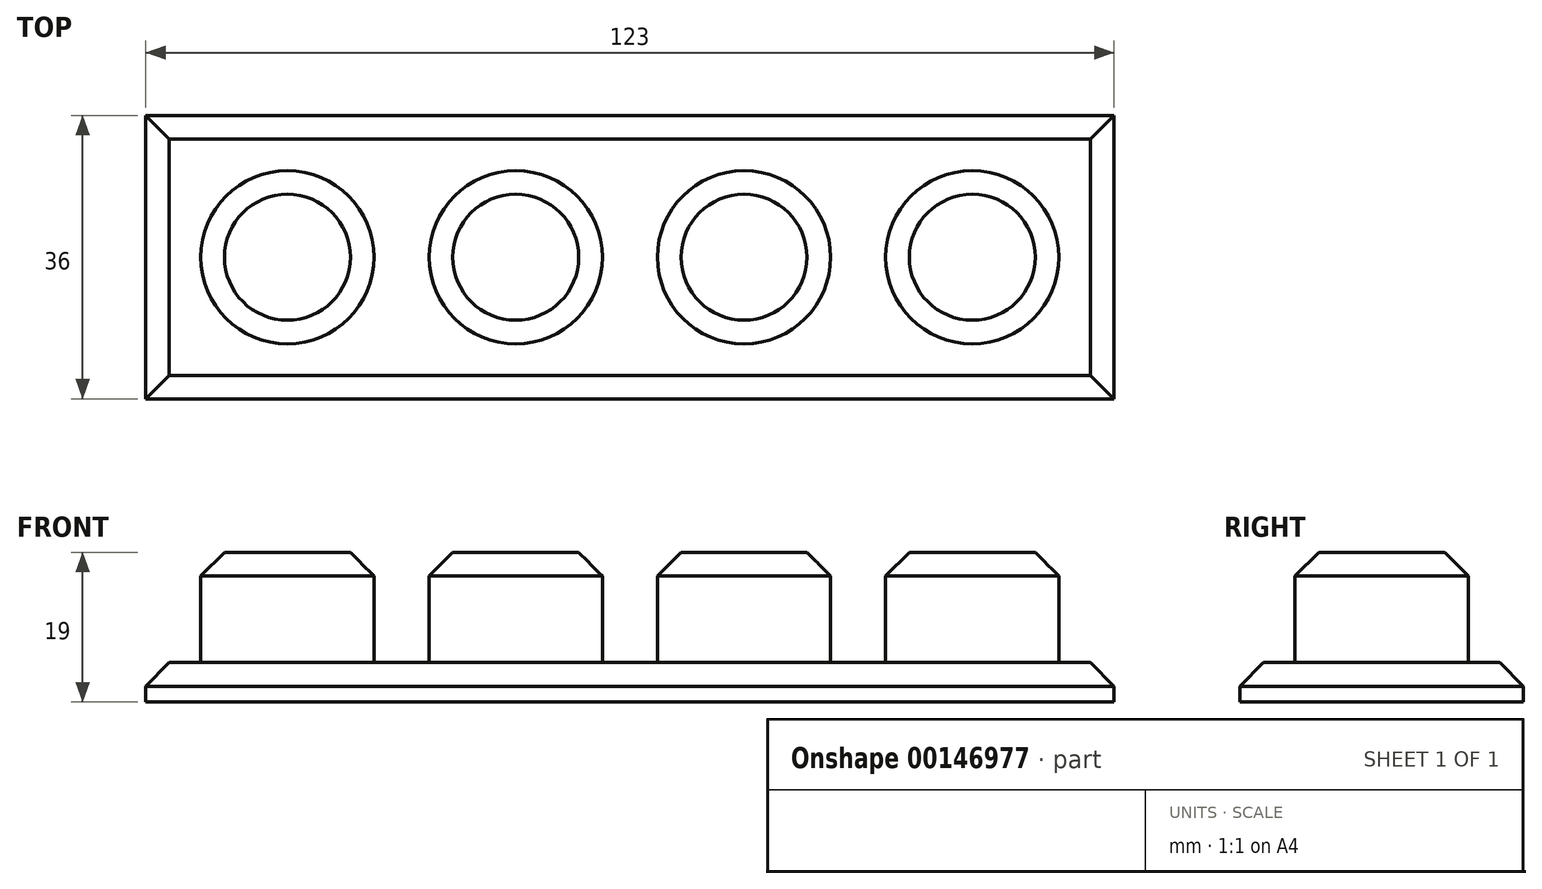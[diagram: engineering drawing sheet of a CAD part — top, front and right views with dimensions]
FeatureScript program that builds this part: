
annotation { "Feature Type Name" : "Feature", "Feature Type Description" : "" }
export const myFeature = defineFeature(function(context is Context, id is Id, definition is map)
    precondition{}
    {
        {
            var Q0;
            Q0=qCreatedBy(makeId("Top.planeOp"),FACE);
            var sketch = newSketch(context, id + "F0", { "sketchPlane" : qUnion([Q0])});
            skLineSegment(sketch, "E0.bottom", {"start": v(-61.57, 25.5) * mm, "end": v(61.43, 25.5) * mm});
            skLineSegment(sketch, "E0.top", {"start": v(-61.57, -10.5) * mm, "end": v(61.43, -10.5) * mm});
            skLineSegment(sketch, "E0.left", {"start": v(-61.57, 25.5) * mm, "end": v(-61.57, -10.5) * mm});
            skLineSegment(sketch, "E0.right", {"start": v(61.43, 25.5) * mm, "end": v(61.43, -10.5) * mm});
            skLineSegment(sketch, "E1", {"start": v(-61.57, 7.5) * mm, "end": v(61.43, 7.5) * mm, "construction": true});
            skCircle(sketch, "E2", {"center": v(-43.57, 7.5) * mm, "radius": 11 * mm});
            skCircle(sketch, "E3", {"center": v(-14.57, 7.5) * mm, "radius": 11 * mm});
            skCircle(sketch, "E4", {"center": v(14.43, 7.5) * mm, "radius": 11 * mm});
            skCircle(sketch, "E5", {"center": v(43.43, 7.5) * mm, "radius": 11 * mm});
            skSolve(sketch);
        }
        {
            var Q0;
            Q0=makeQuery(id+"F0.imprint","IMPRINT",FACE,{"disambiguationData":[TD([[makeQuery(id+"F0.imprint","IMPRINT",EDGE,{"derivedFrom":sQuery(id+"F0.wireOp",EDGE,"E0.bottom")}),-1.0]])]});
            var Q1;
            Q1=makeQuery(id+"F0.imprint","IMPRINT",FACE,{"disambiguationData":[TD([[makeQuery(id+"F0.imprint","IMPRINT",EDGE,{"derivedFrom":sQuery(id+"F0.wireOp",EDGE,"E2")}),1.0]])]});
            var Q2;
            Q2=makeQuery(id+"F0.imprint","IMPRINT",FACE,{"disambiguationData":[TD([[makeQuery(id+"F0.imprint","IMPRINT",EDGE,{"derivedFrom":sQuery(id+"F0.wireOp",EDGE,"E3")}),1.0]])]});
            var Q3;
            Q3=makeQuery(id+"F0.imprint","IMPRINT",FACE,{"disambiguationData":[TD([[makeQuery(id+"F0.imprint","IMPRINT",EDGE,{"derivedFrom":sQuery(id+"F0.wireOp",EDGE,"E4")}),1.0]])]});
            var Q4;
            Q4=makeQuery(id+"F0.imprint","IMPRINT",FACE,{"disambiguationData":[TD([[makeQuery(id+"F0.imprint","IMPRINT",EDGE,{"derivedFrom":sQuery(id+"F0.wireOp",EDGE,"E5")}),1.0]])]});
            extrude(context, id + "F1", {"entities" : qUnion([Q0, Q1, Q2, Q3, Q4]), "depth" : 5 * mm});
        }
        {
            var Q0;
            Q0=makeQuery(id+"F0.imprint","IMPRINT",FACE,{"disambiguationData":[TD([[makeQuery(id+"F0.imprint","IMPRINT",EDGE,{"derivedFrom":sQuery(id+"F0.wireOp",EDGE,"E2")}),1.0]])]});
            var Q1;
            Q1=makeQuery(id+"F0.imprint","IMPRINT",FACE,{"disambiguationData":[TD([[makeQuery(id+"F0.imprint","IMPRINT",EDGE,{"derivedFrom":sQuery(id+"F0.wireOp",EDGE,"E3")}),1.0]])]});
            var Q2;
            Q2=makeQuery(id+"F0.imprint","IMPRINT",FACE,{"disambiguationData":[TD([[makeQuery(id+"F0.imprint","IMPRINT",EDGE,{"derivedFrom":sQuery(id+"F0.wireOp",EDGE,"E4")}),1.0]])]});
            var Q3;
            Q3=makeQuery(id+"F0.imprint","IMPRINT",FACE,{"disambiguationData":[TD([[makeQuery(id+"F0.imprint","IMPRINT",EDGE,{"derivedFrom":sQuery(id+"F0.wireOp",EDGE,"E5")}),1.0]])]});
            extrude(context, id + "F2", {"entities" : qUnion([Q0, Q1, Q2, Q3]), "operationType" : NewBodyOperationType.ADD, "oppositeDirection" : true, "depth" : 14 * mm});
        }
        {
            var Q0;
            Q0=makeQuery(id+"F1.opExtrude","CAP_EDGE",EDGE,{"disambiguationData":[OSD([sQuery(id+"F0.wireOp",EDGE,"E0.bottom")])],"isStart":true});
            var Q1;
            Q1=makeQuery(id+"F1.opExtrude","CAP_EDGE",EDGE,{"disambiguationData":[OSD([sQuery(id+"F0.wireOp",EDGE,"E0.left")])],"isStart":true});
            var Q2;
            Q2=makeQuery(id+"F1.opExtrude","CAP_EDGE",EDGE,{"disambiguationData":[OSD([sQuery(id+"F0.wireOp",EDGE,"E0.right")])],"isStart":true});
            var Q3;
            Q3=makeQuery(id+"F1.opExtrude","CAP_EDGE",EDGE,{"disambiguationData":[OSD([sQuery(id+"F0.wireOp",EDGE,"E0.top")])],"isStart":true});
            var Q4;
            Q4=makeQuery(id+"F2.opExtrude","CAP_EDGE",EDGE,{"disambiguationData":[OSD([sQuery(id+"F0.wireOp",EDGE,"E5")])],"isStart":false});
            var Q5;
            Q5=makeQuery(id+"F2.opExtrude","CAP_EDGE",EDGE,{"disambiguationData":[OSD([sQuery(id+"F0.wireOp",EDGE,"E4")])],"isStart":false});
            var Q6;
            Q6=makeQuery(id+"F2.opExtrude","CAP_EDGE",EDGE,{"disambiguationData":[OSD([sQuery(id+"F0.wireOp",EDGE,"E3")])],"isStart":false});
            var Q7;
            Q7=makeQuery(id+"F2.opExtrude","CAP_EDGE",EDGE,{"disambiguationData":[OSD([sQuery(id+"F0.wireOp",EDGE,"E2")])],"isStart":false});
            chamfer(context, id + "F3", {"entities" : qUnion([Q0, Q1, Q2, Q3, Q4, Q5, Q6, Q7]), "width" : 3 * mm, "tangentPropagation" : true});
        }
        {
            var Q0;
            Q0=makeQuery(id+"F1.opExtrude","SWEPT_BODY",BODY,{"disambiguationData":[OSD([sQuery(id+"F0.wireOp",EDGE,"E0.bottom"),sQuery(id+"F0.wireOp",EDGE,"E0.top"),sQuery(id+"F0.wireOp",EDGE,"E0.left"),sQuery(id+"F0.wireOp",EDGE,"E0.right")])]});
            var Q1;
            Q1=sQuery(id+"F0.wireOp",EDGE,"E1");
            transform(context, id + "F4", {"entities" : qUnion([Q0]), "transformType" : TransformType.ROTATION, "transformAxis" : qUnion([Q1]), "angle" : 180 * degree, "makeCopy" : false});
        }
    });
